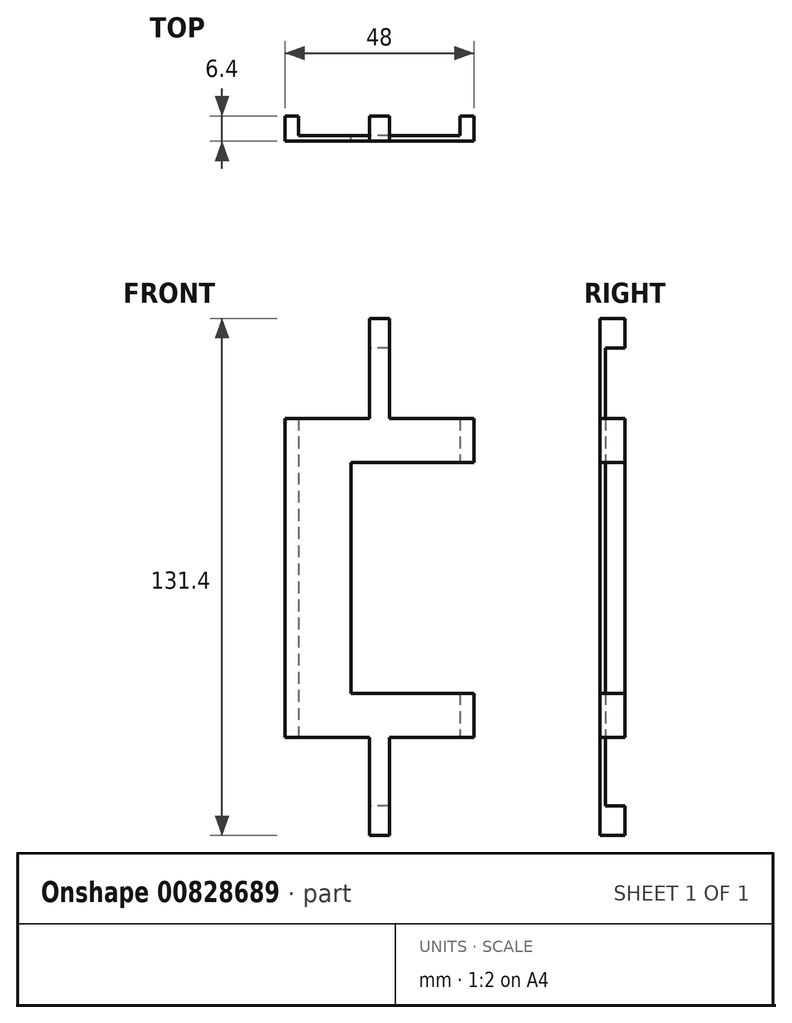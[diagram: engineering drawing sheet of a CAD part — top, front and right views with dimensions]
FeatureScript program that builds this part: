
annotation { "Feature Type Name" : "Feature", "Feature Type Description" : "" }
export const myFeature = defineFeature(function(context is Context, id is Id, definition is map)
    precondition{}
    {
        {
            var Q0;
            Q0=qCreatedBy(makeId("Front.planeOp"),FACE);
            var sketch = newSketch(context, id + "F0", { "sketchPlane" : qUnion([Q0])});
            skLineSegment(sketch, "E0.bottom", {"start": v(-35.5, 58.7) * mm, "end": v(4.6, 58.7) * mm});
            skLineSegment(sketch, "E0.top", {"start": v(-35.5, -56.7) * mm, "end": v(4.6, -56.7) * mm});
            skLineSegment(sketch, "E0.left", {"start": v(-35.5, 58.7) * mm, "end": v(-35.5, -56.7) * mm});
            skLineSegment(sketch, "E0.right", {"start": v(4.6, 58.7) * mm, "end": v(4.6, -56.7) * mm});
            skLineSegment(sketch, "E1.bottom", {"start": v(4.6, 28.8) * mm, "end": v(-19.8, 28.8) * mm});
            skLineSegment(sketch, "E1.top", {"start": v(4.6, -26.8) * mm, "end": v(-19.8, -26.8) * mm});
            skLineSegment(sketch, "E1.left", {"start": v(4.6, 28.8) * mm, "end": v(4.6, -26.8) * mm});
            skLineSegment(sketch, "E1.right", {"start": v(-19.8, 28.8) * mm, "end": v(-19.8, -26.8) * mm});
            skLineSegment(sketch, "E2.bottom", {"start": v(-35.5, 58.7) * mm, "end": v(-20, 58.7) * mm});
            skLineSegment(sketch, "E2.top", {"start": v(-35.5, 43.2) * mm, "end": v(-20, 43.2) * mm});
            skLineSegment(sketch, "E2.left", {"start": v(-35.5, 58.7) * mm, "end": v(-35.5, 43.2) * mm});
            skLineSegment(sketch, "E2.right", {"start": v(-20, 58.7) * mm, "end": v(-20, 43.2) * mm});
            skLineSegment(sketch, "E3.bottom", {"start": v(4.6, 58.7) * mm, "end": v(-10.9, 58.7) * mm});
            skLineSegment(sketch, "E3.top", {"start": v(4.6, 43.2) * mm, "end": v(-10.9, 43.2) * mm});
            skLineSegment(sketch, "E3.left", {"start": v(4.6, 58.7) * mm, "end": v(4.6, 43.2) * mm});
            skLineSegment(sketch, "E3.right", {"start": v(-10.9, 58.7) * mm, "end": v(-10.9, 43.2) * mm});
            skLineSegment(sketch, "E4.bottom", {"start": v(-35.5, -56.7) * mm, "end": v(-20, -56.7) * mm});
            skLineSegment(sketch, "E4.top", {"start": v(-35.5, -41.2) * mm, "end": v(-20, -41.2) * mm});
            skLineSegment(sketch, "E4.left", {"start": v(-35.5, -56.7) * mm, "end": v(-35.5, -41.2) * mm});
            skLineSegment(sketch, "E4.right", {"start": v(-20, -56.7) * mm, "end": v(-20, -41.2) * mm});
            skLineSegment(sketch, "E5.bottom", {"start": v(4.6, -56.7) * mm, "end": v(-10.9, -56.7) * mm});
            skLineSegment(sketch, "E5.top", {"start": v(4.6, -41.2) * mm, "end": v(-10.9, -41.2) * mm});
            skLineSegment(sketch, "E5.left", {"start": v(4.6, -56.7) * mm, "end": v(4.6, -41.2) * mm});
            skLineSegment(sketch, "E5.right", {"start": v(-10.9, -56.7) * mm, "end": v(-10.9, -41.2) * mm});
            skSolve(sketch);
        }
        {
            var Q0;
            Q0=qCreatedBy(makeId("Front.planeOp"),FACE);
            var sketch = newSketch(context, id + "F1", { "sketchPlane" : qUnion([Q0])});
            skLineSegment(sketch, "E6.bottom", {"start": v(-39.4, 41.25) * mm, "end": v(8.6, 41.25) * mm});
            skLineSegment(sketch, "E6.top", {"start": v(-39.4, 30.12) * mm, "end": v(8.6, 30.12) * mm});
            skLineSegment(sketch, "E6.left", {"start": v(-39.4, 41.25) * mm, "end": v(-39.4, 30.12) * mm});
            skLineSegment(sketch, "E6.right", {"start": v(8.6, 41.25) * mm, "end": v(8.6, 30.12) * mm});
            skLineSegment(sketch, "E7.bottom", {"start": v(-39.4, -28.59) * mm, "end": v(8.6, -28.59) * mm});
            skLineSegment(sketch, "E7.top", {"start": v(-39.4, -39.72) * mm, "end": v(8.6, -39.72) * mm});
            skLineSegment(sketch, "E7.left", {"start": v(-39.4, -28.59) * mm, "end": v(-39.4, -39.72) * mm});
            skLineSegment(sketch, "E7.right", {"start": v(8.6, -28.59) * mm, "end": v(8.6, -39.72) * mm});
            skLineSegment(sketch, "E8.bottom", {"start": v(-39.4, 30.12) * mm, "end": v(-22.6, 30.12) * mm});
            skLineSegment(sketch, "E8.top", {"start": v(-39.4, -28.59) * mm, "end": v(-22.6, -28.59) * mm});
            skLineSegment(sketch, "E8.left", {"start": v(-39.4, 30.12) * mm, "end": v(-39.4, -28.59) * mm});
            skLineSegment(sketch, "E8.right", {"start": v(-22.6, 30.12) * mm, "end": v(-22.6, -28.59) * mm});
            skLineSegment(sketch, "E9.bottom", {"start": v(-18, 41.25) * mm, "end": v(-12.9, 41.25) * mm});
            skLineSegment(sketch, "E9.top", {"start": v(-18, 66.7) * mm, "end": v(-12.9, 66.7) * mm});
            skLineSegment(sketch, "E9.left", {"start": v(-18, 41.25) * mm, "end": v(-18, 66.7) * mm});
            skLineSegment(sketch, "E9.right", {"start": v(-12.9, 41.25) * mm, "end": v(-12.9, 66.7) * mm});
            skLineSegment(sketch, "E10.bottom", {"start": v(-18, -39.72) * mm, "end": v(-12.9, -39.72) * mm});
            skLineSegment(sketch, "E10.top", {"start": v(-18, -64.7) * mm, "end": v(-12.9, -64.7) * mm});
            skLineSegment(sketch, "E10.left", {"start": v(-18, -39.72) * mm, "end": v(-18, -64.7) * mm});
            skLineSegment(sketch, "E10.right", {"start": v(-12.9, -39.72) * mm, "end": v(-12.9, -64.7) * mm});
            skSolve(sketch);
        }
        {
            var Q0;
            Q0 = qSketchRegion(id + "F1", true);
            extrude(context, id + "F2", {"entities" : qUnion([Q0]), "depth" : 1.4 * mm, "offsetDistance" : 25 * mm});
        }
        {
            var Q0;
            Q0=makeQuery(id+"F2.opExtrude","CAP_FACE",FACE,{"disambiguationData":[OSD([sQuery(id+"F1.wireOp",EDGE,"E6.bottom"),sQuery(id+"F1.wireOp",EDGE,"E6.top"),sQuery(id+"F1.wireOp",EDGE,"E6.left"),sQuery(id+"F1.wireOp",EDGE,"E6.right"),sQuery(id+"F1.wireOp",EDGE,"E7.bottom"),sQuery(id+"F1.wireOp",EDGE,"E7.top"),sQuery(id+"F1.wireOp",EDGE,"E7.left"),sQuery(id+"F1.wireOp",EDGE,"E7.right"),sQuery(id+"F1.wireOp",EDGE,"E8.left"),sQuery(id+"F1.wireOp",EDGE,"E8.right"),sQuery(id+"F1.wireOp",EDGE,"E9.top"),sQuery(id+"F1.wireOp",EDGE,"E9.left"),sQuery(id+"F1.wireOp",EDGE,"E9.right"),sQuery(id+"F1.wireOp",EDGE,"E10.top"),sQuery(id+"F1.wireOp",EDGE,"E10.left"),sQuery(id+"F1.wireOp",EDGE,"E10.right")])],"isStart":true});
            var sketch = newSketch(context, id + "F3", { "sketchPlane" : qUnion([Q0])});
            skLineSegment(sketch, "E11.bottom", {"start": v(12.9, 66.7) * mm, "end": v(18, 66.7) * mm});
            skLineSegment(sketch, "E11.top", {"start": v(12.9, 59.2) * mm, "end": v(18, 59.2) * mm});
            skLineSegment(sketch, "E11.left", {"start": v(12.9, 66.7) * mm, "end": v(12.9, 59.2) * mm});
            skLineSegment(sketch, "E11.right", {"start": v(18, 66.7) * mm, "end": v(18, 59.2) * mm});
            skLineSegment(sketch, "E12.bottom", {"start": v(-8.6, 41.25) * mm, "end": v(-5.1, 41.25) * mm});
            skLineSegment(sketch, "E12.top", {"start": v(-8.6, 30.12) * mm, "end": v(-5.1, 30.12) * mm});
            skLineSegment(sketch, "E12.left", {"start": v(-8.6, 41.25) * mm, "end": v(-8.6, 30.12) * mm});
            skLineSegment(sketch, "E12.right", {"start": v(-5.1, 41.25) * mm, "end": v(-5.1, 30.12) * mm});
            skLineSegment(sketch, "E13.bottom", {"start": v(39.4, 41.25) * mm, "end": v(36, 41.25) * mm});
            skLineSegment(sketch, "E13.top", {"start": v(39.4, -39.72) * mm, "end": v(36, -39.72) * mm});
            skLineSegment(sketch, "E13.left", {"start": v(39.4, 41.25) * mm, "end": v(39.4, -39.72) * mm});
            skLineSegment(sketch, "E13.right", {"start": v(36, 41.25) * mm, "end": v(36, -39.72) * mm});
            skLineSegment(sketch, "E14.bottom", {"start": v(-8.6, -28.59) * mm, "end": v(-5.1, -28.59) * mm});
            skLineSegment(sketch, "E14.top", {"start": v(-8.6, -39.72) * mm, "end": v(-5.1, -39.72) * mm});
            skLineSegment(sketch, "E14.left", {"start": v(-8.6, -28.59) * mm, "end": v(-8.6, -39.72) * mm});
            skLineSegment(sketch, "E14.right", {"start": v(-5.1, -28.59) * mm, "end": v(-5.1, -39.72) * mm});
            skLineSegment(sketch, "E15.bottom", {"start": v(12.9, -64.7) * mm, "end": v(18, -64.7) * mm});
            skLineSegment(sketch, "E15.top", {"start": v(12.9, -57.2) * mm, "end": v(18, -57.2) * mm});
            skLineSegment(sketch, "E15.left", {"start": v(12.9, -64.7) * mm, "end": v(12.9, -57.2) * mm});
            skLineSegment(sketch, "E15.right", {"start": v(18, -64.7) * mm, "end": v(18, -57.2) * mm});
            skSolve(sketch);
        }
        {
            var Q0;
            Q0 = qSketchRegion(id + "F3", true);
            extrude(context, id + "F4", {"entities" : qUnion([Q0]), "operationType" : NewBodyOperationType.ADD, "depth" : 5 * mm, "offsetDistance" : 25 * mm});
        }
    });
